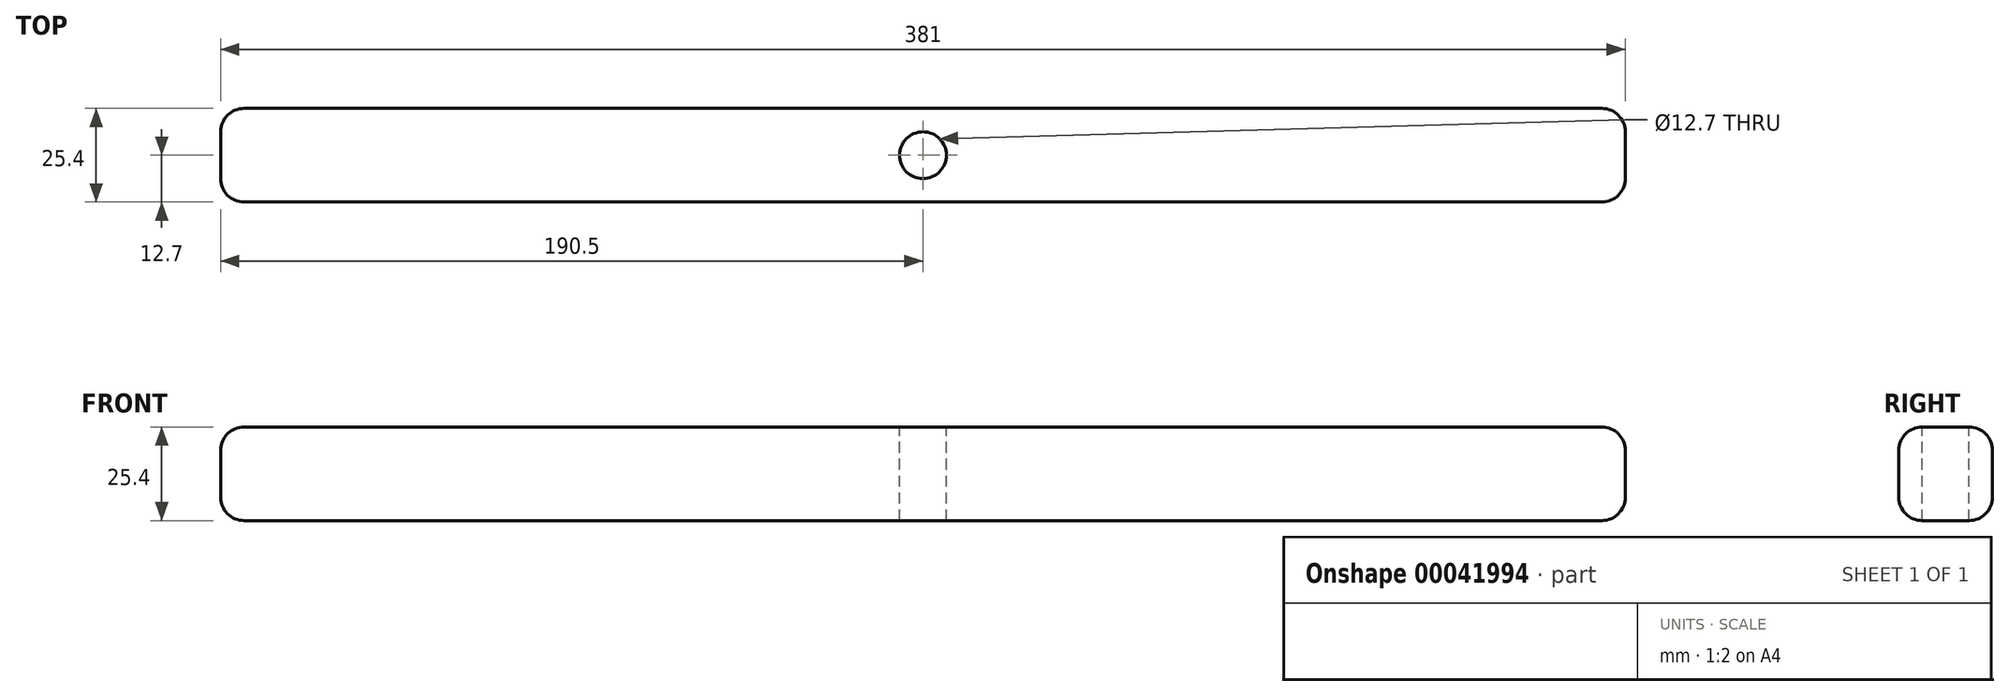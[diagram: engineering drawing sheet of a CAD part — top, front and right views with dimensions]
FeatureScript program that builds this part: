
annotation { "Feature Type Name" : "Feature", "Feature Type Description" : "" }
export const myFeature = defineFeature(function(context is Context, id is Id, definition is map)
    precondition{}
    {
        {
            var Q0;
            Q0=qCreatedBy(makeId("Right.planeOp"),FACE);
            var sketch = newSketch(context, id + "F0", { "sketchPlane" : qUnion([Q0])});
            skLineSegment(sketch, "E0.rect.bottom", {"start": v(12.7, 12.7) * mm, "end": v(-12.7, 12.7) * mm});
            skLineSegment(sketch, "E0.rect.top", {"start": v(12.7, -12.7) * mm, "end": v(-12.7, -12.7) * mm});
            skLineSegment(sketch, "E0.rect.left", {"start": v(12.7, 12.7) * mm, "end": v(12.7, -12.7) * mm});
            skLineSegment(sketch, "E0.rect.right", {"start": v(-12.7, 12.7) * mm, "end": v(-12.7, -12.7) * mm});
            skPoint(sketch, "E0.rect.middle", {"position": v(0, 0) * mm});
            skSolve(sketch);
        }
        {
            var Q0;
            Q0=makeQuery(id+"F0.imprint","IMPRINT",FACE,{"disambiguationData":[TD([[makeQuery(id+"F0.imprint","IMPRINT",EDGE,{"derivedFrom":sQuery(id+"F0.wireOp",EDGE,"E0.rect.bottom")}),1.0]])]});
            extrude(context, id + "F1", {"entities" : qUnion([Q0]), "depth" : 304.8 * mm, "hasSecondDirection" : true, "secondDirectionOppositeDirection" : true, "secondDirectionDepth" : 76.2 * mm});
        }
        {
            var Q0;
            Q0=makeQuery(id+"F1.opExtrude","SWEPT_EDGE",EDGE,{"disambiguationData":[OSD([sQuery(id+"F0.wireOp",EDGE,"E0.rect.bottom"),sQuery(id+"F0.wireOp",EDGE,"E0.rect.right")])]});
            var Q1;
            Q1=makeQuery(id+"F1.opExtrude","SWEPT_EDGE",EDGE,{"disambiguationData":[OSD([sQuery(id+"F0.wireOp",EDGE,"E0.rect.bottom"),sQuery(id+"F0.wireOp",EDGE,"E0.rect.left")])]});
            var Q2;
            Q2=makeQuery(id+"F1.opExtrude","SWEPT_EDGE",EDGE,{"disambiguationData":[OSD([sQuery(id+"F0.wireOp",EDGE,"E0.rect.top"),sQuery(id+"F0.wireOp",EDGE,"E0.rect.right")])]});
            var Q3;
            Q3=makeQuery(id+"F1.opExtrude","SWEPT_EDGE",EDGE,{"disambiguationData":[OSD([sQuery(id+"F0.wireOp",EDGE,"E0.rect.top"),sQuery(id+"F0.wireOp",EDGE,"E0.rect.left")])]});
            var Q4;
            Q4=makeQuery(id+"F1.opExtrude","CAP_FACE",FACE,{"disambiguationData":[OSD([sQuery(id+"F0.wireOp",EDGE,"E0.rect.bottom"),sQuery(id+"F0.wireOp",EDGE,"E0.rect.top"),sQuery(id+"F0.wireOp",EDGE,"E0.rect.left"),sQuery(id+"F0.wireOp",EDGE,"E0.rect.right")])],"isStart":false});
            var Q5;
            Q5=makeQuery(id+"F1.opExtrude","CAP_FACE",FACE,{"disambiguationData":[OSD([sQuery(id+"F0.wireOp",EDGE,"E0.rect.bottom"),sQuery(id+"F0.wireOp",EDGE,"E0.rect.top"),sQuery(id+"F0.wireOp",EDGE,"E0.rect.left"),sQuery(id+"F0.wireOp",EDGE,"E0.rect.right")])],"isStart":true});
            fillet(context, id + "F2", {"entities" : qUnion([Q0, Q1, Q2, Q3, Q4, Q5]), "radius" : 6.35 * mm, "tangentPropagation" : true, "allowEdgeOverflow" : false});
        }
        {
            var Q0;
            Q0=makeQuery(id+"F1.opExtrude","SWEPT_FACE",FACE,{"disambiguationData":[OSD([sQuery(id+"F0.wireOp",EDGE,"E0.rect.bottom")])]});
            var sketch = newSketch(context, id + "F3", { "sketchPlane" : qUnion([Q0])});
            skCircle(sketch, "E1", {"center": v(114.3, 0) * mm, "radius": 6.35 * mm});
            skPoint(sketch, "E1.centerSnap0", {"position": v(-69.85, 0) * mm});
            skSolve(sketch);
        }
        {
            var Q0;
            {var subQ0=sQuery(id+"F3.wireOp",EDGE,"E1");var subQ1=sQuery(id+"F0.wireOp",EDGE,"E0.rect.bottom");var subQ2=makeQuery(id+"F1.opExtrude","SWEPT_FACE",FACE,{"disambiguationData":[OSD([subQ1])]});var subQ4=makeQuery(id+"F3.imprint","INTERSECT",VERTEX,{"derivedFrom":[makeQuery(id+"F2.opFillet","BLEND_EDGE",EDGE,{"blendedFrom":[makeQuery(id+"F1.opExtrude","SWEPT_EDGE",EDGE,{"disambiguationData":[OSD([subQ1,sQuery(id+"F0.wireOp",EDGE,"E0.rect.left")])]}),subQ2],"blendedInto":[subQ2]}),subQ0]});Q0=makeQuery(id+"F3.imprint","IMPRINT",FACE,{"disambiguationData":[TD([[makeQuery(id+"F3.imprint","IMPRINT",EDGE,{"disambiguationData":[TD([[subQ4,-1.0]])],"derivedFrom":subQ0}),1.0]])]});}
            extrude(context, id + "F4", {"entities" : qUnion([Q0]), "operationType" : NewBodyOperationType.REMOVE, "endBound" : BoundingType.THROUGH_ALL, "oppositeDirection" : true, "depth" : 25.4 * mm});
        }
    });
